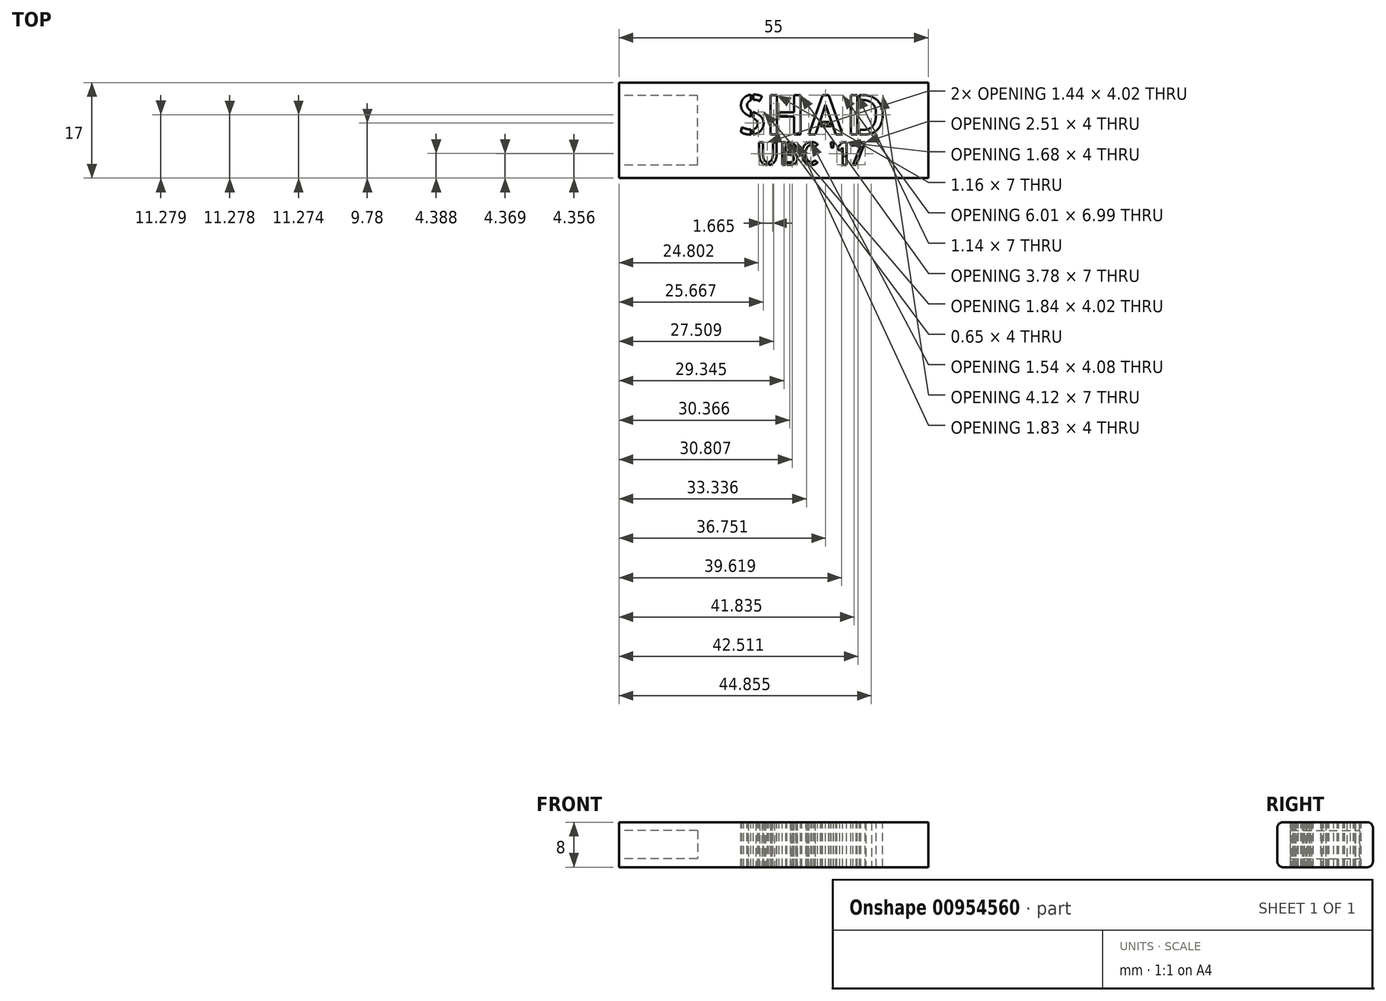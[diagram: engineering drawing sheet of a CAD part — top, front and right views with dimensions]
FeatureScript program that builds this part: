
annotation { "Feature Type Name" : "Feature", "Feature Type Description" : "" }
export const myFeature = defineFeature(function(context is Context, id is Id, definition is map)
    precondition{}
    {
        {
            var Q0;
            Q0=qCreatedBy(makeId("Front.planeOp"),FACE);
            var sketch = newSketch(context, id + "F0", { "sketchPlane" : qUnion([Q0])});
            skLineSegment(sketch, "E0.bottom", {"start": v(8.5, -4) * mm, "end": v(-8.5, -4) * mm});
            skLineSegment(sketch, "E0.top", {"start": v(8.5, 4) * mm, "end": v(-8.5, 4) * mm});
            skLineSegment(sketch, "E0.left", {"start": v(8.5, -4) * mm, "end": v(8.5, 4) * mm});
            skLineSegment(sketch, "E0.right", {"start": v(-8.5, -4) * mm, "end": v(-8.5, 4) * mm});
            skPoint(sketch, "E0.middle", {"position": v(0, 0) * mm});
            skSolve(sketch);
        }
        {
            var Q0;
            Q0 = qSketchRegion(id + "F0", true);
            extrude(context, id + "F1", {"entities" : qUnion([Q0]), "depth" : 55 * mm, "offsetDistance" : 25 * mm});
        }
        {
            var Q0;
            Q0=makeQuery(id+"F1.opExtrude","SWEPT_EDGE",EDGE,{"disambiguationData":[OSD([sQuery(id+"F0.wireOp",EDGE,"E0.bottom"),sQuery(id+"F0.wireOp",EDGE,"E0.left")])]});
            fillet(context, id + "F2", {"entities" : qUnion([Q0]), "radius" : 1 * mm, "tangentPropagation" : true, "allowEdgeOverflow" : false});
        }
        {
            var Q0;
            Q0=makeQuery(id+"F1.opExtrude","SWEPT_EDGE",EDGE,{"disambiguationData":[OSD([sQuery(id+"F0.wireOp",EDGE,"E0.top"),sQuery(id+"F0.wireOp",EDGE,"E0.left")])]});
            fillet(context, id + "F3", {"entities" : qUnion([Q0]), "radius" : 1 * mm, "tangentPropagation" : true, "allowEdgeOverflow" : false});
        }
        {
            var Q0;
            Q0=makeQuery(id+"F1.opExtrude","SWEPT_EDGE",EDGE,{"disambiguationData":[OSD([sQuery(id+"F0.wireOp",EDGE,"E0.top"),sQuery(id+"F0.wireOp",EDGE,"E0.right")])]});
            var Q1;
            Q1=makeQuery(id+"F1.opExtrude","SWEPT_EDGE",EDGE,{"disambiguationData":[OSD([sQuery(id+"F0.wireOp",EDGE,"E0.bottom"),sQuery(id+"F0.wireOp",EDGE,"E0.right")])]});
            fillet(context, id + "F4", {"entities" : qUnion([Q0, Q1]), "radius" : 1 * mm, "tangentPropagation" : true, "allowEdgeOverflow" : false});
        }
        {
            var Q0;
            Q0=makeQuery(id+"F1.opExtrude","CAP_FACE",FACE,{"disambiguationData":[OSD([sQuery(id+"F0.wireOp",EDGE,"E0.bottom"),sQuery(id+"F0.wireOp",EDGE,"E0.top"),sQuery(id+"F0.wireOp",EDGE,"E0.left"),sQuery(id+"F0.wireOp",EDGE,"E0.right")])],"isStart":false});
            var sketch = newSketch(context, id + "F5", { "sketchPlane" : qUnion([Q0])});
            skLineSegment(sketch, "E1.bottom", {"start": v(6.2, 2.5) * mm, "end": v(-6.2, 2.5) * mm});
            skLineSegment(sketch, "E1.top", {"start": v(6.2, -2.5) * mm, "end": v(-6.2, -2.5) * mm});
            skLineSegment(sketch, "E1.left", {"start": v(6.2, 2.5) * mm, "end": v(6.2, -2.5) * mm});
            skLineSegment(sketch, "E1.right", {"start": v(-6.2, 2.5) * mm, "end": v(-6.2, -2.5) * mm});
            skPoint(sketch, "E1.middle", {"position": v(0, 0) * mm});
            skSolve(sketch);
        }
        {
            var Q0;
            Q0=makeQuery(id+"F5.imprint","IMPRINT",FACE,{"disambiguationData":[TD([[makeQuery(id+"F5.imprint","IMPRINT",EDGE,{"derivedFrom":sQuery(id+"F5.wireOp",EDGE,"E1.bottom")}),1.0]])]});
            extrude(context, id + "F6", {"entities" : qUnion([Q0]), "operationType" : NewBodyOperationType.REMOVE, "oppositeDirection" : true, "depth" : 14 * mm, "offsetDistance" : 25 * mm});
        }
        {
            var Q0;
            Q0=makeQuery(id+"F1.opExtrude","SWEPT_BODY",BODY,{"disambiguationData":[OSD([sQuery(id+"F0.wireOp",EDGE,"E0.bottom"),sQuery(id+"F0.wireOp",EDGE,"E0.top"),sQuery(id+"F0.wireOp",EDGE,"E0.left"),sQuery(id+"F0.wireOp",EDGE,"E0.right")])]});
            var Q1;
            Q1=makeQuery(id+"F1.opExtrude","CAP_EDGE",EDGE,{"disambiguationData":[OSD([sQuery(id+"F0.wireOp",EDGE,"E0.left")])],"isStart":false});
            transform(context, id + "F7", {"entities" : qUnion([Q0]), "transformType" : TransformType.ROTATION, "transformAxis" : qUnion([Q1]), "angle" : 270 * degree, "makeCopy" : false});
        }
        {
            var Q0;
            Q0=makeQuery(id+"F1.opExtrude","SWEPT_FACE",FACE,{"disambiguationData":[OSD([sQuery(id+"F0.wireOp",EDGE,"E0.top")])]});
            var sketch = newSketch(context, id + "F8", { "sketchPlane" : qUnion([Q0])});
            skText(sketch, "E2", { "text": "SHAD", "fontName": "AllertaStencil-Regular.ttf"});
            skText(sketch, "E3", { "text": "UBC \'17", "fontName": "AllertaStencil-Regular.ttf"});
            skText(sketch, "E4", { "text": "UBC \'17", "fontName": "AllertaStencil-Regular.ttf"});
            const initialGuessF8  = {"E2": [0.02939, -0.04722, 1, 0, 0.007], "E3": [0.0801, -0.10357, 1, 0, 0.004], "E4": [0.033, -0.05263, 1, 0, 0.004]};
            skSetInitialGuess(sketch, initialGuessF8);
            skSolve(sketch);
        }
        {
            var Q0;
            Q0 = qSketchRegion(id + "F8", true);
            extrude(context, id + "F9", {"entities" : qUnion([Q0]), "operationType" : NewBodyOperationType.REMOVE, "oppositeDirection" : true, "depth" : 25 * mm, "offsetDistance" : 25 * mm});
        }
    });
